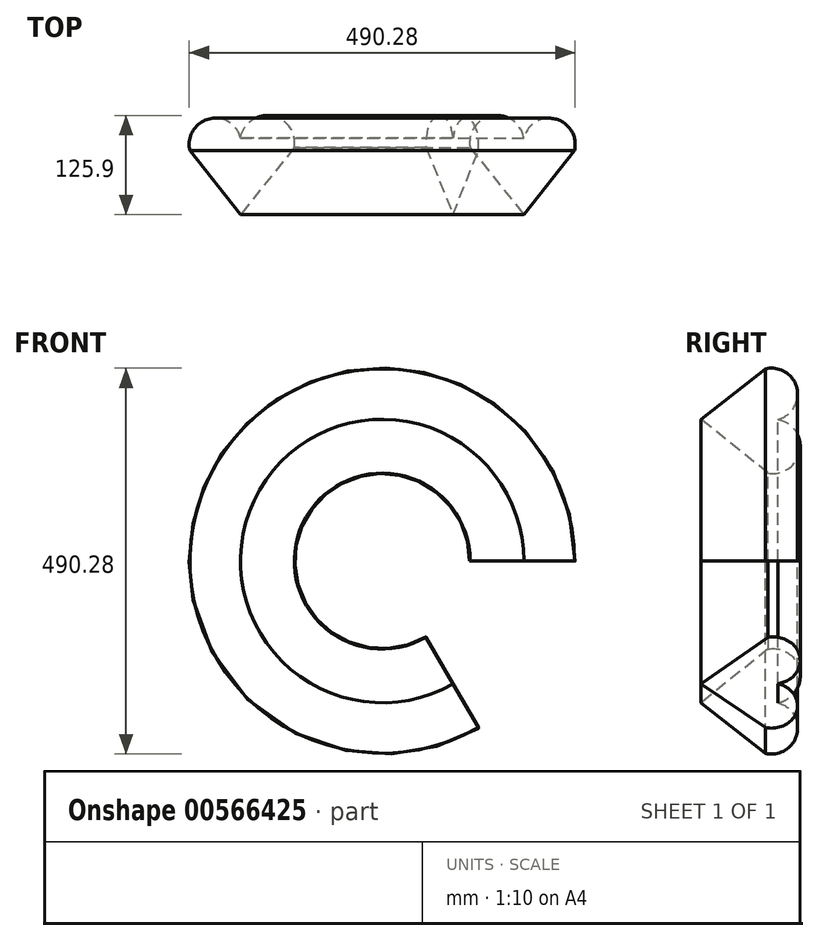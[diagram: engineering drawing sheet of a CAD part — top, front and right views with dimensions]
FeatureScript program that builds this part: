
annotation { "Feature Type Name" : "Feature", "Feature Type Description" : "" }
export const myFeature = defineFeature(function(context is Context, id is Id, definition is map)
    precondition{}
    {
        {
            var Q0;
            Q0=qCreatedBy(makeId("Top.planeOp"),FACE);
            var sketch = newSketch(context, id + "F0", { "sketchPlane" : qUnion([Q0])});
            skLineSegment(sketch, "E0", {"start": v(-68.34, 37.8) * mm, "end": v(0, -47.18) * mm});
            skLineSegment(sketch, "E1", {"start": v(0, -47.18) * mm, "end": v(64.15, 34.36) * mm});
            skArc(sketch, "E2", {"start": v(0, 50.2) * mm, "mid": v(-40.37, 78.16) * mm, "end": v(-68.34, 37.8) * mm});
            skArc(sketch, "E3", {"start": v(64.15, 34.36) * mm, "mid": v(40, 74.36) * mm, "end": v(0, 50.2) * mm});
            skSolve(sketch);
        }
        {
            var Q0;
            Q0=qCreatedBy(makeId("Top.planeOp"),FACE);
            var sketch = newSketch(context, id + "F1", { "sketchPlane" : qUnion([Q0])});
            skLineSegment(sketch, "E4", {"start": v(-180.03, 34.17) * mm, "end": v(-180.03, -71.48) * mm});
            skSolve(sketch);
        }
        {
            var Q0;
            Q0=makeQuery(id+"F0.imprint","IMPRINT",FACE,{"disambiguationData":[TD([[makeQuery(id+"F0.imprint","IMPRINT",EDGE,{"derivedFrom":sQuery(id+"F0.wireOp",EDGE,"E0")}),1.0]])]});
            var Q1;
            Q1=sQuery(id+"F1.wireOp",EDGE,"E4");
            revolve(context, id + "F2", {"entities" : qUnion([Q0]), "axis" : qUnion([Q1]), "revolveType" : RevolveType.ONE_DIRECTION, "angle" : 300 * degree});
        }
    });
